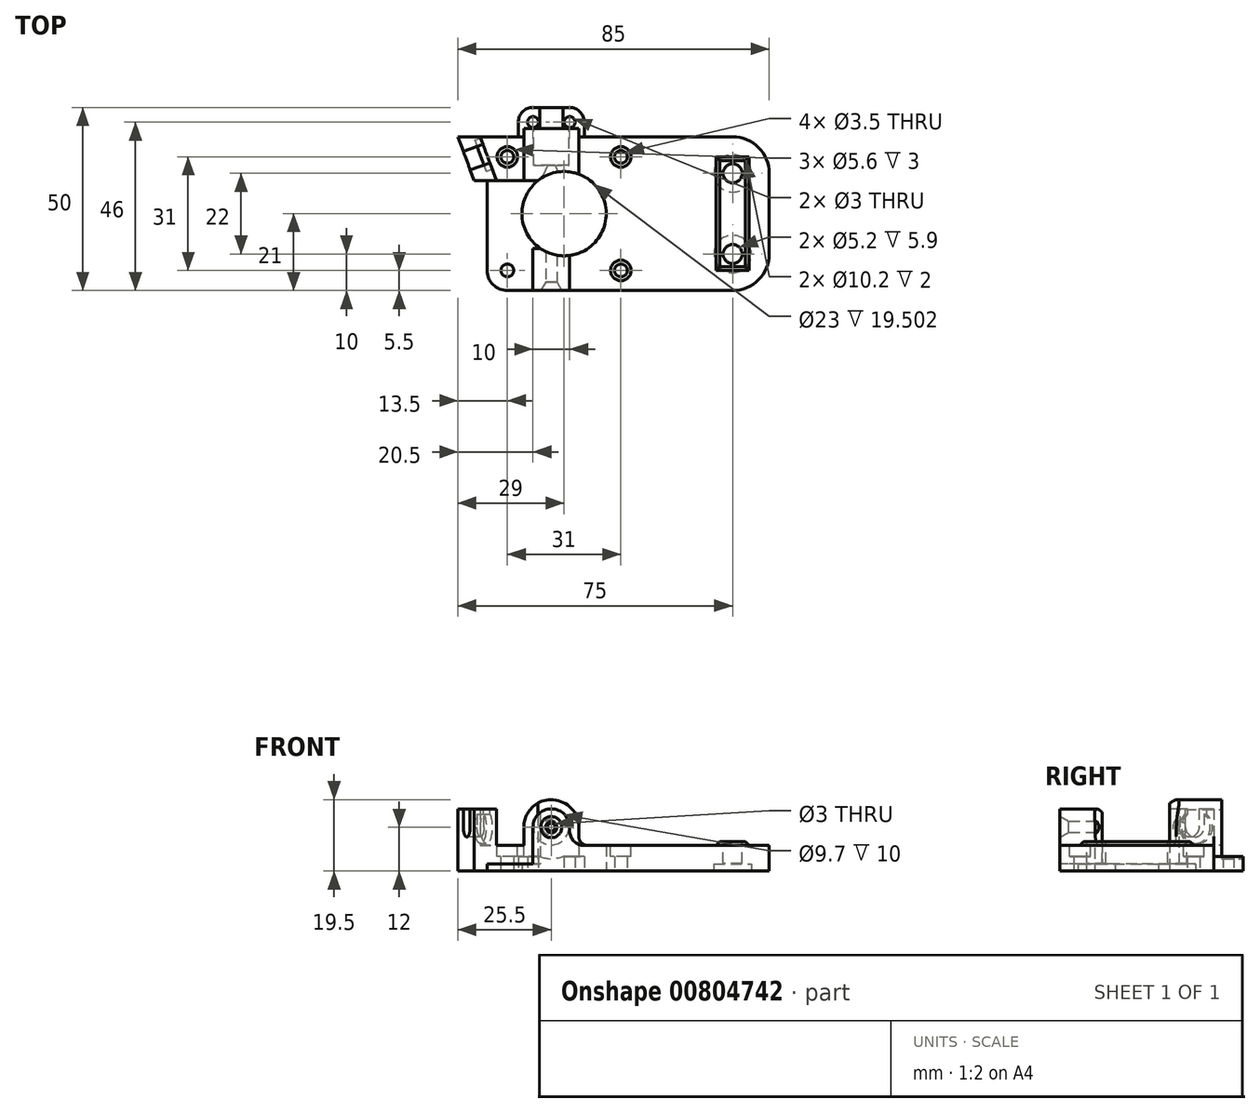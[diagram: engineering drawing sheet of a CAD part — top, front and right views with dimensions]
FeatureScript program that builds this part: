
annotation { "Feature Type Name" : "Feature", "Feature Type Description" : "" }
export const myFeature = defineFeature(function(context is Context, id is Id, definition is map)
    precondition{}
    {
        {
            var Q0;
            Q0=qCreatedBy(makeId("Top.planeOp"),FACE);
            var sketch = newSketch(context, id + "F0", { "sketchPlane" : qUnion([Q0])});
            skLineSegment(sketch, "E0.bottom", {"start": v(42.5, -21) * mm, "end": v(-34.5, -21) * mm});
            skLineSegment(sketch, "E0.top", {"start": v(42.5, 21) * mm, "end": v(-42.5, 21) * mm});
            skLineSegment(sketch, "E0.left", {"start": v(42.5, -21) * mm, "end": v(42.5, 21) * mm});
            skPoint(sketch, "E0.middle", {"position": v(0, 0) * mm});
            skLineSegment(sketch, "E1", {"start": v(-42.5, 21) * mm, "end": v(-38.06, 9) * mm});
            skLineSegment(sketch, "E2", {"start": v(-38.06, 9) * mm, "end": v(-34.5, 9) * mm});
            skLineSegment(sketch, "E3", {"start": v(-34.5, 9) * mm, "end": v(-34.5, -21) * mm});
            skPoint(sketch, "E4.orphan", {"position": v(-42.5, -21) * mm});
            skSolve(sketch);
        }
        {
            var Q0;
            Q0=makeQuery(id+"F0.imprint","IMPRINT",FACE,{"disambiguationData":[TD([[makeQuery(id+"F0.imprint","IMPRINT",EDGE,{"derivedFrom":sQuery(id+"F0.wireOp",EDGE,"E0.bottom")}),-1.0]])]});
            extrude(context, id + "F1", {"entities" : qUnion([Q0]), "depth" : 7 * mm, "offsetDistance" : 25 * mm});
        }
        {
            var Q0;
            Q0=makeQuery(id+"F1.opExtrude","SWEPT_FACE",FACE,{"disambiguationData":[OSD([sQuery(id+"F0.wireOp",EDGE,"E0.bottom")])]});
            var Q1;
            Q1=makeQuery(id+"F1.opExtrude","SWEPT_FACE",FACE,{"disambiguationData":[OSD([sQuery(id+"F0.wireOp",EDGE,"E0.top")])]});
            cPlane(context, id + "F2", {"entities" : qUnion([Q0, Q1]), "cplaneType" : CPlaneType.MID_PLANE, "offset" : 25 * mm, "width" : 150 * mm, "height" : 150 * mm});
        }
        {
            var Q0;
            Q0=makeQuery(id+"F1.opExtrude","SWEPT_FACE",FACE,{"disambiguationData":[OSD([sQuery(id+"F0.wireOp",EDGE,"E0.bottom")])]});
            var sketch = newSketch(context, id + "F3", { "sketchPlane" : qUnion([Q0])});
            skLineSegment(sketch, "E5", {"start": v(-22, 0) * mm, "end": v(-22, 12) * mm});
            skArc(sketch, "E6", {"start": v(-22, 12) * mm, "mid": v(-17, 17) * mm, "end": v(-12, 12) * mm});
            skLineSegment(sketch, "E7", {"start": v(-12, 12) * mm, "end": v(-12, 0) * mm});
            skLineSegment(sketch, "E8", {"start": v(-12, 0) * mm, "end": v(-22, 0) * mm});
            skSolve(sketch);
        }
        {
            var Q0;
            Q0=qSketchRegion(id+"F3",true);
            var Q1;
            Q1=qCreatedBy(id+"F2.planeOp",FACE);
            extrude(context, id + "F4", {"entities" : qUnion([Q0]), "operationType" : NewBodyOperationType.ADD, "endBound" : BoundingType.UP_TO_SURFACE, "oppositeDirection" : true, "depth" : 25 * mm, "endBoundEntityFace" : qUnion([Q1]), "offsetDistance" : 25 * mm});
        }
        {
            var Q0;
            Q0=makeQuery(id+"F4.boolean.opBoolean","MERGE",FACE,{"derivedFrom":[makeQuery(id+"F1.opExtrude","SWEPT_FACE",FACE,{"disambiguationData":[OSD([sQuery(id+"F0.wireOp",EDGE,"E0.bottom")])]}),makeQuery(id+"F4.opExtrude","CAP_FACE",FACE,{"disambiguationData":[OSD([sQuery(id+"F3.wireOp",EDGE,"E5"),sQuery(id+"F3.wireOp",EDGE,"E6"),sQuery(id+"F3.wireOp",EDGE,"E7"),sQuery(id+"F3.wireOp",EDGE,"E8")])],"isStart":true})]});
            var sketch = newSketch(context, id + "F5", { "sketchPlane" : qUnion([Q0])});
            skPoint(sketch, "E9", {"position": v(-17, 12) * mm});
            skSolve(sketch);
        }
        {
            var Q0;
            Q0=sQuery(id+"F5.wireOp",VERTEX,"E9");
            var Q1;
            Q1=makeQuery(id+"F1.opExtrude","SWEPT_BODY",BODY,{"disambiguationData":[OSD([sQuery(id+"F0.wireOp",EDGE,"E0.bottom"),sQuery(id+"F0.wireOp",EDGE,"E0.top"),sQuery(id+"F0.wireOp",EDGE,"E0.left"),sQuery(id+"F0.wireOp",EDGE,"E1"),sQuery(id+"F0.wireOp",EDGE,"E2"),sQuery(id+"F0.wireOp",EDGE,"E3")])]});
            hole(context, id + "F6", {"style" : HoleStyle.C_SINK, "endStyle" : HoleEndStyle.THROUGH, "standardTappedOrClearance" : lookupTablePath({ "standard" : "ISO", "size" : "3", "type" : "Drilled" }), "standardBlindInLast" : lookupTablePath({ "standard" : "ISO", "size" : "3", "type" : "Drilled" }), "holeDiameter" : 3 * mm, "cSinkDiameter" : 5.76 * mm, "cSinkAngle" : 60 * degree, "isTappedThrough" : true, "tappedDepth" : 12 * mm, "tapClearance" : 3, "locations" : qUnion([Q0]), "scope" : qUnion([Q1])});
        }
        {
            var Q0;
            Q0=qCreatedBy(id+"F2.planeOp",FACE);
            var sketch = newSketch(context, id + "F7", { "sketchPlane" : qUnion([Q0])});
            skLineSegment(sketch, "E10", {"start": v(-24.5, 0) * mm, "end": v(-24.5, 12) * mm});
            skArc(sketch, "E11", {"start": v(-24.5, 12) * mm, "mid": v(-17, 19.5) * mm, "end": v(-9.5, 12) * mm});
            skLineSegment(sketch, "E12", {"start": v(-9.5, 12) * mm, "end": v(-9.5, 0) * mm});
            skLineSegment(sketch, "E13", {"start": v(-9.5, 0) * mm, "end": v(-24.5, 0) * mm});
            skSolve(sketch);
        }
        {
            var Q0;
            Q0=makeQuery(id+"F7.imprint","IMPRINT",FACE,{"disambiguationData":[TD([[makeQuery(id+"F7.imprint","IMPRINT",EDGE,{"derivedFrom":sQuery(id+"F7.wireOp",EDGE,"E10")}),-1.0]])]});
            var Q1;
            Q1=sQuery(id+"F7.wireOp",EDGE,"E11");
            extrude(context, id + "F8", {"entities" : qUnion([Q0]), "operationType" : NewBodyOperationType.ADD, "surfaceEntities" : qUnion([Q1]), "oppositeDirection" : true, "depth" : 23.2 * mm, "offsetDistance" : 25 * mm});
        }
        {
            var Q0;
            Q0=makeQuery(id+"F8.boolean.opBoolean","MERGE",FACE,{"derivedFrom":[makeQuery(id+"F1.opExtrude","CAP_FACE",FACE,{"disambiguationData":[OSD([sQuery(id+"F0.wireOp",EDGE,"E0.bottom"),sQuery(id+"F0.wireOp",EDGE,"E0.top"),sQuery(id+"F0.wireOp",EDGE,"E0.left"),sQuery(id+"F0.wireOp",EDGE,"E1"),sQuery(id+"F0.wireOp",EDGE,"E2"),sQuery(id+"F0.wireOp",EDGE,"E3")])],"isStart":true}),makeQuery(id+"F8.opExtrude","SWEPT_FACE",FACE,{"disambiguationData":[OSD([sQuery(id+"F7.wireOp",EDGE,"E13")])]})]});
            var sketch = newSketch(context, id + "F9", { "sketchPlane" : qUnion([Q0])});
            skLineSegment(sketch, "E14", {"start": v(-8, -21) * mm, "end": v(-8, -29) * mm});
            skLineSegment(sketch, "E15", {"start": v(-8, -29) * mm, "end": v(-26, -29) * mm});
            skLineSegment(sketch, "E16", {"start": v(-26, -29) * mm, "end": v(-26, -21) * mm});
            skLineSegment(sketch, "E17", {"start": v(-8, -21) * mm, "end": v(-26, -21) * mm});
            skCircle(sketch, "E18", {"center": v(-12, -25) * mm, "radius": 1.5 * mm});
            skCircle(sketch, "E19", {"center": v(-22, -25) * mm, "radius": 1.5 * mm});
            skLineSegment(sketch, "E20", {"start": v(-12, -25) * mm, "end": v(-22, -25) * mm, "construction": true});
            skLineSegment(sketch, "E21", {"start": v(-17, -29) * mm, "end": v(-17, -25) * mm, "construction": true});
            skSolve(sketch);
        }
        {
            var Q0;
            {var subQ4=sQuery(id+"F9.wireOp",EDGE,"E14");Q0=makeQuery(id+"F9.imprint","IMPRINT",FACE,{"disambiguationData":[TD([[makeQuery(id+"F9.imprint","IMPRINT",EDGE,{"derivedFrom":subQ4}),-1.0]])]});}
            extrude(context, id + "F10", {"entities" : qUnion([Q0]), "operationType" : NewBodyOperationType.ADD, "oppositeDirection" : true, "depth" : 4 * mm, "offsetDistance" : 25 * mm});
        }
        {
            var Q0;
            Q0=makeQuery(id+"F10.opExtrude","SWEPT_FACE",FACE,{"disambiguationData":[OSD([sQuery(id+"F9.wireOp",EDGE,"E15")])]});
            var sketch = newSketch(context, id + "F11", { "sketchPlane" : qUnion([Q0])});
            skCircle(sketch, "E22", {"center": v(17, 12) * mm, "radius": 8.6 * mm});
            skSolve(sketch);
        }
        {
            var Q0;
            Q0=qSketchRegion(id+"F11",true);
            var Q1;
            Q1=makeQuery(id+"F8.opExtrude","CAP_FACE",FACE,{"disambiguationData":[OSD([sQuery(id+"F7.wireOp",EDGE,"E10"),sQuery(id+"F7.wireOp",EDGE,"E11"),sQuery(id+"F7.wireOp",EDGE,"E12"),sQuery(id+"F7.wireOp",EDGE,"E13")])],"isStart":false});
            extrude(context, id + "F12", {"entities" : qUnion([Q0]), "operationType" : NewBodyOperationType.REMOVE, "endBound" : BoundingType.UP_TO_SURFACE, "oppositeDirection" : true, "depth" : 25 * mm, "endBoundEntityFace" : qUnion([Q1]), "offsetDistance" : 25 * mm});
        }
        {
            var Q0;
            {var subQ0=sQuery(id+"F7.wireOp",EDGE,"E13");var subQ1=sQuery(id+"F7.wireOp",EDGE,"E12");var subQ2=sQuery(id+"F7.wireOp",EDGE,"E11");var subQ3=sQuery(id+"F7.wireOp",EDGE,"E10");Q0=makeQuery(id+"F12.boolean.opBoolean","MERGE",FACE,{"derivedFrom":[makeQuery(id+"F8.opExtrude","CAP_FACE",FACE,{"disambiguationData":[OSD([subQ3,subQ2,subQ1,subQ0])],"isStart":false}),makeQuery(id+"F12.opExtrude","CAP_FACE",FACE,{"disambiguationData":[OSD([subQ3,subQ2,subQ1,subQ0])],"isStart":false})]});}
            var sketch = newSketch(context, id + "F13", { "sketchPlane" : qUnion([Q0])});
            skCircle(sketch, "E23", {"center": v(17, 12) * mm, "radius": 4.85 * mm});
            skSolve(sketch);
        }
        {
            var Q0;
            Q0=qSketchRegion(id+"F13",true);
            extrude(context, id + "F14", {"entities" : qUnion([Q0]), "operationType" : NewBodyOperationType.REMOVE, "oppositeDirection" : true, "depth" : 10 * mm, "offsetDistance" : 25 * mm});
        }
        {
            var Q0;
            {var subQ0=sQuery(id+"F0.wireOp",EDGE,"E2");var subQ2=sQuery(id+"F0.wireOp",EDGE,"E0.top");var subQ4=sQuery(id+"F0.wireOp",EDGE,"E1");var subQ5=sQuery(id+"F0.wireOp",EDGE,"E0.bottom");var subQ6=sQuery(id+"F0.wireOp",EDGE,"E3");Q0=makeQuery(id+"F8.boolean.opBoolean","SPLIT",FACE,{"disambiguationData":[TD([makeQuery(id+"F1.opExtrude","SWEPT_FACE",FACE,{"disambiguationData":[OSD([subQ4])]})])],"derivedFrom":makeQuery(id+"F1.opExtrude","CAP_FACE",FACE,{"disambiguationData":[OSD([subQ5,subQ2,sQuery(id+"F0.wireOp",EDGE,"E0.left"),subQ4,subQ0,subQ6])],"isStart":false})});}
            var sketch = newSketch(context, id + "F15", { "sketchPlane" : qUnion([Q0])});
            skLineSegment(sketch, "E24", {"start": v(-42.5, 21) * mm, "end": v(-36.42, 21) * mm});
            skLineSegment(sketch, "E25", {"start": v(-36.42, 21) * mm, "end": v(-31.98, 9) * mm});
            skLineSegment(sketch, "E26", {"start": v(-31.98, 9) * mm, "end": v(-38.06, 9) * mm});
            skLineSegment(sketch, "E27", {"start": v(-38.06, 9) * mm, "end": v(-42.5, 21) * mm});
            skSolve(sketch);
        }
        {
            var Q0;
            Q0=qSketchRegion(id+"F15",true);
            extrude(context, id + "F16", {"entities" : qUnion([Q0]), "operationType" : NewBodyOperationType.ADD, "depth" : 10 * mm, "offsetDistance" : 25 * mm});
        }
        {
            var Q0;
            Q0=makeQuery(id+"F16.boolean.opBoolean","MERGE",FACE,{"derivedFrom":[makeQuery(id+"F1.opExtrude","SWEPT_FACE",FACE,{"disambiguationData":[OSD([sQuery(id+"F0.wireOp",EDGE,"E1")])]}),makeQuery(id+"F16.opExtrude","SWEPT_FACE",FACE,{"disambiguationData":[OSD([sQuery(id+"F15.wireOp",EDGE,"E27")])]})]});
            var sketch = newSketch(context, id + "F17", { "sketchPlane" : qUnion([Q0])});
            skLineSegment(sketch, "E28", {"start": v(-30.14, 17) * mm, "end": v(-30.14, 12) * mm});
            skArc(sketch, "E29", {"start": v(-30.14, 12) * mm, "mid": v(-27.44, 9.3) * mm, "end": v(-24.74, 12) * mm});
            skLineSegment(sketch, "E30", {"start": v(-24.74, 12) * mm, "end": v(-24.74, 17) * mm});
            skLineSegment(sketch, "E31", {"start": v(-30.14, 17) * mm, "end": v(-24.74, 17) * mm});
            skSolve(sketch);
        }
        {
            var Q0;
            Q0=qSketchRegion(id+"F17",true);
            extrude(context, id + "F18", {"entities" : qUnion([Q0]), "operationType" : NewBodyOperationType.REMOVE, "endBound" : BoundingType.UP_TO_NEXT, "oppositeDirection" : true, "depth" : 25 * mm, "offsetDistance" : 25 * mm});
        }
        {
            var Q0;
            Q0=makeQuery(id+"F16.opExtrude","SWEPT_FACE",FACE,{"disambiguationData":[OSD([sQuery(id+"F15.wireOp",EDGE,"E25")])]});
            var sketch = newSketch(context, id + "F19", { "sketchPlane" : qUnion([Q0])});
            skCircle(sketch, "E32", {"center": v(27.44, 12) * mm, "radius": 4.5 * mm});
            skSolve(sketch);
        }
        {
            var Q0;
            Q0=qSketchRegion(id+"F19",true);
            var Q1;
            Q1=makeQuery(id+"F16.boolean.opBoolean","MERGE",FACE,{"derivedFrom":[makeQuery(id+"F1.opExtrude","SWEPT_FACE",FACE,{"disambiguationData":[OSD([sQuery(id+"F0.wireOp",EDGE,"E1")])]}),makeQuery(id+"F16.opExtrude","SWEPT_FACE",FACE,{"disambiguationData":[OSD([sQuery(id+"F15.wireOp",EDGE,"E27")])]})]});
            extrude(context, id + "F20", {"entities" : qUnion([Q0]), "operationType" : NewBodyOperationType.REMOVE, "endBound" : BoundingType.UP_TO_SURFACE, "oppositeDirection" : true, "depth" : .5 * mm, "endBoundEntityFace" : qUnion([Q1]), "hasOffset" : true, "offsetDistance" : 4 * mm});
        }
        {
            var Q0;
            {var subQ1=sQuery(id+"F0.wireOp",EDGE,"E0.left");var subQ2=sQuery(id+"F0.wireOp",EDGE,"E0.top");var subQ4=sQuery(id+"F0.wireOp",EDGE,"E0.bottom");Q0=makeQuery(id+"F8.boolean.opBoolean","SPLIT",FACE,{"disambiguationData":[TD([makeQuery(id+"F1.opExtrude","SWEPT_FACE",FACE,{"disambiguationData":[OSD([subQ1])]})])],"derivedFrom":makeQuery(id+"F1.opExtrude","CAP_FACE",FACE,{"disambiguationData":[OSD([subQ4,subQ2,subQ1,sQuery(id+"F0.wireOp",EDGE,"E1"),sQuery(id+"F0.wireOp",EDGE,"E2"),sQuery(id+"F0.wireOp",EDGE,"E3")])],"isStart":false})});}
            var sketch = newSketch(context, id + "F21", { "sketchPlane" : qUnion([Q0])});
            skLineSegment(sketch, "E33.bottom", {"start": v(37, -15.5) * mm, "end": v(28, -15.5) * mm});
            skLineSegment(sketch, "E33.top", {"start": v(37, 15.5) * mm, "end": v(28, 15.5) * mm});
            skLineSegment(sketch, "E33.left", {"start": v(37, -15.5) * mm, "end": v(37, 15.5) * mm});
            skLineSegment(sketch, "E33.right", {"start": v(28, -15.5) * mm, "end": v(28, 15.5) * mm});
            skPoint(sketch, "E33.middle", {"position": v(32.5, 0) * mm});
            skSolve(sketch);
        }
        {
            var Q0;
            Q0=qSketchRegion(id+"F21",true);
            extrude(context, id + "F22", {"entities" : qUnion([Q0]), "operationType" : NewBodyOperationType.ADD, "depth" : 1 * mm, "offsetDistance" : 25 * mm});
        }
        {
            var Q0;
            Q0=makeQuery(id+"F22.opExtrude","CAP_EDGE",EDGE,{"disambiguationData":[OSD([sQuery(id+"F21.wireOp",EDGE,"E33.left")])],"isStart":false});
            var Q1;
            Q1=makeQuery(id+"F22.opExtrude","CAP_EDGE",EDGE,{"disambiguationData":[OSD([sQuery(id+"F21.wireOp",EDGE,"E33.top")])],"isStart":false});
            var Q2;
            Q2=makeQuery(id+"F22.opExtrude","CAP_EDGE",EDGE,{"disambiguationData":[OSD([sQuery(id+"F21.wireOp",EDGE,"E33.right")])],"isStart":false});
            var Q3;
            Q3=makeQuery(id+"F22.opExtrude","CAP_EDGE",EDGE,{"disambiguationData":[OSD([sQuery(id+"F21.wireOp",EDGE,"E33.bottom")])],"isStart":false});
            chamfer(context, id + "F23", {"entities" : qUnion([Q0, Q1, Q2, Q3]), "width" : 1 * mm, "tangentPropagation" : true});
        }
        {
            var Q0;
            Q0=makeQuery(id+"F22.opExtrude","CAP_FACE",FACE,{"disambiguationData":[OSD([sQuery(id+"F21.wireOp",EDGE,"E33.bottom"),sQuery(id+"F21.wireOp",EDGE,"E33.top"),sQuery(id+"F21.wireOp",EDGE,"E33.left"),sQuery(id+"F21.wireOp",EDGE,"E33.right")])],"isStart":false});
            var sketch = newSketch(context, id + "F24", { "sketchPlane" : qUnion([Q0])});
            skCircle(sketch, "E34", {"center": v(32.5, -11) * mm, "radius": 2.6 * mm});
            skPoint(sketch, "E34.centerSnap0", {"position": v(32.5, -14.5) * mm});
            skCircle(sketch, "E35", {"center": v(32.5, 11) * mm, "radius": 2.6 * mm});
            skLineSegment(sketch, "E36", {"start": v(32.5, -11) * mm, "end": v(32.5, 11) * mm, "construction": true});
            skLineSegment(sketch, "E37", {"start": v(36, 0) * mm, "end": v(32.5, 0) * mm, "construction": true});
            skSolve(sketch);
        }
        {
            var Q0;
            Q0=qSketchRegion(id+"F24",true);
            extrude(context, id + "F25", {"entities" : qUnion([Q0]), "operationType" : NewBodyOperationType.REMOVE, "oppositeDirection" : true, "depth" : 5.9 * mm, "offsetDistance" : 25 * mm});
        }
        {
            var Q0;
            {var subQ0=sQuery(id+"F7.wireOp",EDGE,"E13");Q0=makeQuery(id+"F10.boolean.opBoolean","MERGE",FACE,{"derivedFrom":[makeQuery(id+"F8.boolean.opBoolean","MERGE",FACE,{"derivedFrom":[makeQuery(id+"F1.opExtrude","CAP_FACE",FACE,{"disambiguationData":[OSD([sQuery(id+"F0.wireOp",EDGE,"E0.bottom"),sQuery(id+"F0.wireOp",EDGE,"E0.top"),sQuery(id+"F0.wireOp",EDGE,"E0.left"),sQuery(id+"F0.wireOp",EDGE,"E1"),sQuery(id+"F0.wireOp",EDGE,"E2"),sQuery(id+"F0.wireOp",EDGE,"E3")])],"isStart":true}),makeQuery(id+"F8.opExtrude","SWEPT_FACE",FACE,{"disambiguationData":[OSD([subQ0])]})]}),makeQuery(id+"F10.opExtrude","CAP_FACE",FACE,{"disambiguationData":[OSD([sQuery(id+"F7.wireOp",EDGE,"E10"),sQuery(id+"F7.wireOp",EDGE,"E12"),subQ0,sQuery(id+"F9.wireOp",EDGE,"E14"),sQuery(id+"F9.wireOp",EDGE,"E15"),sQuery(id+"F9.wireOp",EDGE,"E16"),sQuery(id+"F9.wireOp",EDGE,"E17"),sQuery(id+"F9.wireOp",EDGE,"E18"),sQuery(id+"F9.wireOp",EDGE,"E19")])],"isStart":true})]});}
            var sketch = newSketch(context, id + "F26", { "sketchPlane" : qUnion([Q0])});
            skCircle(sketch, "E38", {"center": v(32.5, -11) * mm, "radius": 5.1 * mm});
            skCircle(sketch, "E39", {"center": v(32.5, 11) * mm, "radius": 5.1 * mm});
            skSolve(sketch);
        }
        {
            var Q0;
            Q0=qSketchRegion(id+"F26",true);
            extrude(context, id + "F27", {"entities" : qUnion([Q0]), "operationType" : NewBodyOperationType.REMOVE, "oppositeDirection" : true, "depth" : 2 * mm, "offsetDistance" : 25 * mm});
        }
        {
            var Q0;
            {var subQ0=sQuery(id+"F7.wireOp",EDGE,"E13");Q0=makeQuery(id+"F10.boolean.opBoolean","MERGE",FACE,{"derivedFrom":[makeQuery(id+"F8.boolean.opBoolean","MERGE",FACE,{"derivedFrom":[makeQuery(id+"F1.opExtrude","CAP_FACE",FACE,{"disambiguationData":[OSD([sQuery(id+"F0.wireOp",EDGE,"E0.bottom"),sQuery(id+"F0.wireOp",EDGE,"E0.top"),sQuery(id+"F0.wireOp",EDGE,"E0.left"),sQuery(id+"F0.wireOp",EDGE,"E1"),sQuery(id+"F0.wireOp",EDGE,"E2"),sQuery(id+"F0.wireOp",EDGE,"E3")])],"isStart":true}),makeQuery(id+"F8.opExtrude","SWEPT_FACE",FACE,{"disambiguationData":[OSD([subQ0])]})]}),makeQuery(id+"F10.opExtrude","CAP_FACE",FACE,{"disambiguationData":[OSD([sQuery(id+"F7.wireOp",EDGE,"E10"),sQuery(id+"F7.wireOp",EDGE,"E12"),subQ0,sQuery(id+"F9.wireOp",EDGE,"E14"),sQuery(id+"F9.wireOp",EDGE,"E15"),sQuery(id+"F9.wireOp",EDGE,"E16"),sQuery(id+"F9.wireOp",EDGE,"E17"),sQuery(id+"F9.wireOp",EDGE,"E18"),sQuery(id+"F9.wireOp",EDGE,"E19")])],"isStart":true})]});}
            var sketch = newSketch(context, id + "F28", { "sketchPlane" : qUnion([Q0])});
            skLineSegment(sketch, "E40.bottom", {"start": v(2, -15.5) * mm, "end": v(-29, -15.5) * mm, "construction": true});
            skLineSegment(sketch, "E40.top", {"start": v(2, 15.5) * mm, "end": v(-29, 15.5) * mm, "construction": true});
            skLineSegment(sketch, "E40.left", {"start": v(2, -15.5) * mm, "end": v(2, 15.5) * mm, "construction": true});
            skLineSegment(sketch, "E40.right", {"start": v(-29, -15.5) * mm, "end": v(-29, 15.5) * mm, "construction": true});
            skPoint(sketch, "E40.middle", {"position": v(-13.5, 0) * mm});
            skPoint(sketch, "E41", {"position": v(2, -15.5) * mm});
            skPoint(sketch, "E42", {"position": v(-29, -15.5) * mm});
            skPoint(sketch, "E43", {"position": v(-29, 15.5) * mm});
            skPoint(sketch, "E44", {"position": v(2, 15.5) * mm});
            skSolve(sketch);
        }
        {
            var Q0;
            Q0=sQuery(id+"F28.wireOp",VERTEX,"E41");
            var Q1;
            Q1=sQuery(id+"F28.wireOp",VERTEX,"E42");
            var Q2;
            Q2=sQuery(id+"F28.wireOp",VERTEX,"E43");
            var Q3;
            Q3=sQuery(id+"F28.wireOp",VERTEX,"E44");
            var Q4;
            Q4=makeQuery(id+"F1.opExtrude","SWEPT_BODY",BODY,{"disambiguationData":[OSD([sQuery(id+"F0.wireOp",EDGE,"E0.bottom"),sQuery(id+"F0.wireOp",EDGE,"E0.top"),sQuery(id+"F0.wireOp",EDGE,"E0.left"),sQuery(id+"F0.wireOp",EDGE,"E1"),sQuery(id+"F0.wireOp",EDGE,"E2"),sQuery(id+"F0.wireOp",EDGE,"E3")])]});
            hole(context, id + "F29", {"style" : HoleStyle.SIMPLE, "endStyle" : HoleEndStyle.THROUGH, "standardTappedOrClearance" : lookupTablePath({ "standard" : "ISO", "size" : "3.5", "type" : "Drilled" }), "standardBlindInLast" : lookupTablePath({ "standard" : "ISO", "size" : "3.5", "type" : "Drilled" }), "holeDiameter" : 3.5 * mm, "isTappedThrough" : true, "tappedDepth" : 12 * mm, "tapClearance" : 3, "locations" : qUnion([Q0, Q1, Q2, Q3]), "scope" : qUnion([Q4])});
        }
        {
            var Q0;
            {var subQ1=sQuery(id+"F0.wireOp",EDGE,"E0.left");Q0=makeQuery(id+"F28.imprint","IMPRINT",FACE,{"disambiguationData":[TD([[makeQuery(id+"F28.imprint","IMPRINT",EDGE,{"derivedFrom":makeQuery(id+"F1.opExtrude","CAP_EDGE",EDGE,{"disambiguationData":[OSD([subQ1])],"isStart":true})}),-1.0]])]});}
            var sketch = newSketch(context, id + "F30", { "sketchPlane" : qUnion([Q0])});
            skCircle(sketch, "E45", {"center": v(-13.5, 0) * mm, "radius": 11.5 * mm});
            skSolve(sketch);
        }
        {
            var Q0;
            Q0=qSketchRegion(id+"F30",true);
            extrude(context, id + "F31", {"entities" : qUnion([Q0]), "operationType" : NewBodyOperationType.REMOVE, "endBound" : BoundingType.UP_TO_NEXT, "oppositeDirection" : true, "depth" : 25 * mm, "offsetDistance" : 25 * mm});
        }
        {
            var Q0;
            {var subQ0=sQuery(id+"F0.wireOp",EDGE,"E2");var subQ2=sQuery(id+"F0.wireOp",EDGE,"E0.top");var subQ4=sQuery(id+"F0.wireOp",EDGE,"E1");var subQ5=sQuery(id+"F0.wireOp",EDGE,"E0.bottom");var subQ6=sQuery(id+"F0.wireOp",EDGE,"E3");Q0=makeQuery(id+"F8.boolean.opBoolean","SPLIT",FACE,{"disambiguationData":[TD([makeQuery(id+"F1.opExtrude","SWEPT_FACE",FACE,{"disambiguationData":[OSD([subQ4])]})])],"derivedFrom":makeQuery(id+"F1.opExtrude","CAP_FACE",FACE,{"disambiguationData":[OSD([subQ5,subQ2,sQuery(id+"F0.wireOp",EDGE,"E0.left"),subQ4,subQ0,subQ6])],"isStart":false})});}
            var sketch = newSketch(context, id + "F32", { "sketchPlane" : qUnion([Q0])});
            skLineSegment(sketch, "E46", {"start": v(-34.5, -21) * mm, "end": v(-22, -21) * mm});
            skLineSegment(sketch, "E47", {"start": v(-22, -21) * mm, "end": v(-22, -9.5) * mm});
            skLineSegment(sketch, "E48", {"start": v(-22, -9.5) * mm, "end": v(-13.5, -9.5) * mm});
            skLineSegment(sketch, "E49", {"start": v(-13.5, -9.5) * mm, "end": v(-13.5, 9) * mm});
            skLineSegment(sketch, "E50", {"start": v(-13.5, 9) * mm, "end": v(-34.5, 9) * mm});
            skLineSegment(sketch, "E51", {"start": v(-34.5, 9) * mm, "end": v(-34.5, -21) * mm});
            skSolve(sketch);
        }
        {
            var Q0;
            Q0=qSketchRegion(id+"F32",true);
            var Q1;
            {var subQ0=sQuery(id+"F7.wireOp",EDGE,"E13");Q1=makeQuery(id+"F10.boolean.opBoolean","MERGE",FACE,{"derivedFrom":[makeQuery(id+"F8.boolean.opBoolean","MERGE",FACE,{"derivedFrom":[makeQuery(id+"F1.opExtrude","CAP_FACE",FACE,{"disambiguationData":[OSD([sQuery(id+"F0.wireOp",EDGE,"E0.bottom"),sQuery(id+"F0.wireOp",EDGE,"E0.top"),sQuery(id+"F0.wireOp",EDGE,"E0.left"),sQuery(id+"F0.wireOp",EDGE,"E1"),sQuery(id+"F0.wireOp",EDGE,"E2"),sQuery(id+"F0.wireOp",EDGE,"E3")])],"isStart":true}),makeQuery(id+"F8.opExtrude","SWEPT_FACE",FACE,{"disambiguationData":[OSD([subQ0])]})]}),makeQuery(id+"F10.opExtrude","CAP_FACE",FACE,{"disambiguationData":[OSD([sQuery(id+"F7.wireOp",EDGE,"E10"),sQuery(id+"F7.wireOp",EDGE,"E12"),subQ0,sQuery(id+"F9.wireOp",EDGE,"E14"),sQuery(id+"F9.wireOp",EDGE,"E15"),sQuery(id+"F9.wireOp",EDGE,"E16"),sQuery(id+"F9.wireOp",EDGE,"E17"),sQuery(id+"F9.wireOp",EDGE,"E18"),sQuery(id+"F9.wireOp",EDGE,"E19")])],"isStart":true})]});}
            extrude(context, id + "F33", {"entities" : qUnion([Q0]), "operationType" : NewBodyOperationType.REMOVE, "endBound" : BoundingType.UP_TO_SURFACE, "oppositeDirection" : true, "depth" : 25 * mm, "endBoundEntityFace" : qUnion([Q1]), "hasOffset" : true, "offsetDistance" : 2 * mm, "hasSecondDirection" : true, "secondDirectionBound" : SecondDirectionBoundingType.THROUGH_ALL, "secondDirectionOppositeDirection" : false, "secondDirectionDepth" : 25 * mm});
        }
        {
            var Q0;
            Q0=makeQuery(id+"F14.boolean.opBoolean","COPY",FACE,{"derivedFrom":makeQuery(id+"F14.opExtrude","CAP_FACE",FACE,{"disambiguationData":[OSD([sQuery(id+"F13.wireOp",EDGE,"E23")])],"isStart":false})});
            var sketch = newSketch(context, id + "F34", { "sketchPlane" : qUnion([Q0])});
            skCircle(sketch, "E52", {"center": v(17, 12) * mm, "radius": 1.05 * mm});
            skSolve(sketch);
        }
        {
            var Q0;
            Q0=makeQuery(id+"F34.imprint","IMPRINT",FACE,{"disambiguationData":[TD([[makeQuery(id+"F34.imprint","IMPRINT",EDGE,{"derivedFrom":sQuery(id+"F34.wireOp",EDGE,"E52")}),1.0]])]});
            extrude(context, id + "F35", {"entities" : qUnion([Q0]), "operationType" : NewBodyOperationType.REMOVE, "endBound" : BoundingType.UP_TO_NEXT, "oppositeDirection" : true, "depth" : 25 * mm, "offsetDistance" : 25 * mm, "hasDraft" : true, "draftAngle" : 22.6 * degree});
        }
        {
            var Q0;
            {var subQ1=sQuery(id+"F0.wireOp",EDGE,"E0.left");var subQ2=sQuery(id+"F0.wireOp",EDGE,"E0.top");var subQ4=sQuery(id+"F0.wireOp",EDGE,"E0.bottom");Q0=makeQuery(id+"F8.boolean.opBoolean","SPLIT",FACE,{"disambiguationData":[TD([makeQuery(id+"F1.opExtrude","SWEPT_FACE",FACE,{"disambiguationData":[OSD([subQ1])]})])],"derivedFrom":makeQuery(id+"F1.opExtrude","CAP_FACE",FACE,{"disambiguationData":[OSD([subQ4,subQ2,subQ1,sQuery(id+"F0.wireOp",EDGE,"E1"),sQuery(id+"F0.wireOp",EDGE,"E2"),sQuery(id+"F0.wireOp",EDGE,"E3")])],"isStart":false})});}
            var sketch = newSketch(context, id + "F36", { "sketchPlane" : qUnion([Q0])});
            skCircle(sketch, "E53", {"center": v(2, -15.5) * mm, "radius": 2.8 * mm});
            skCircle(sketch, "E54", {"center": v(2, 15.5) * mm, "radius": 2.8 * mm});
            skCircle(sketch, "E55", {"center": v(-29, 15.5) * mm, "radius": 2.8 * mm});
            skSolve(sketch);
        }
        {
            var Q0;
            Q0=qSketchRegion(id+"F36",true);
            extrude(context, id + "F37", {"entities" : qUnion([Q0]), "operationType" : NewBodyOperationType.REMOVE, "oppositeDirection" : true, "depth" : 3 * mm, "offsetDistance" : 25 * mm});
        }
        {
            var Q0;
            Q0=makeQuery(id+"F4.boolean.opBoolean","INTERSECT",EDGE,{"derivedFrom":[makeQuery(id+"F1.opExtrude","CAP_FACE",FACE,{"disambiguationData":[OSD([sQuery(id+"F0.wireOp",EDGE,"E0.bottom"),sQuery(id+"F0.wireOp",EDGE,"E0.top"),sQuery(id+"F0.wireOp",EDGE,"E0.left"),sQuery(id+"F0.wireOp",EDGE,"E1"),sQuery(id+"F0.wireOp",EDGE,"E2"),sQuery(id+"F0.wireOp",EDGE,"E3")])],"isStart":false}),makeQuery(id+"F4.opExtrude","SWEPT_FACE",FACE,{"disambiguationData":[OSD([sQuery(id+"F3.wireOp",EDGE,"E7")])]})]});
            var Q1;
            Q1=makeQuery(id+"F10.opExtrude","SWEPT_EDGE",EDGE,{"disambiguationData":[OSD([sQuery(id+"F9.wireOp",EDGE,"E14"),sQuery(id+"F9.wireOp",EDGE,"E15")])]});
            var Q2;
            Q2=makeQuery(id+"F10.opExtrude","SWEPT_EDGE",EDGE,{"disambiguationData":[OSD([sQuery(id+"F9.wireOp",EDGE,"E15"),sQuery(id+"F9.wireOp",EDGE,"E16")])]});
            fillet(context, id + "F38", {"entities" : qUnion([Q0, Q1, Q2]), "radius" : 4 * mm, "tangentPropagation" : true, "allowEdgeOverflow" : false});
        }
        {
            var Q0;
            Q0=makeQuery(id+"F1.opExtrude","SWEPT_EDGE",EDGE,{"disambiguationData":[OSD([sQuery(id+"F0.wireOp",EDGE,"E0.bottom"),sQuery(id+"F0.wireOp",EDGE,"E3")])]});
            fillet(context, id + "F39", {"entities" : qUnion([Q0]), "radius" : 5.5 * mm, "tangentPropagation" : true, "allowEdgeOverflow" : false});
        }
        {
            var Q0;
            Q0=makeQuery(id+"F8.boolean.opBoolean","INTERSECT",EDGE,{"derivedFrom":[makeQuery(id+"F1.opExtrude","CAP_FACE",FACE,{"disambiguationData":[OSD([sQuery(id+"F0.wireOp",EDGE,"E0.bottom"),sQuery(id+"F0.wireOp",EDGE,"E0.top"),sQuery(id+"F0.wireOp",EDGE,"E0.left"),sQuery(id+"F0.wireOp",EDGE,"E1"),sQuery(id+"F0.wireOp",EDGE,"E2"),sQuery(id+"F0.wireOp",EDGE,"E3")])],"isStart":false}),makeQuery(id+"F8.opExtrude","SWEPT_FACE",FACE,{"disambiguationData":[OSD([sQuery(id+"F7.wireOp",EDGE,"E12")])]})]});
            fillet(context, id + "F40", {"entities" : qUnion([Q0]), "radius" : 2.5 * mm, "tangentPropagation" : true, "allowEdgeOverflow" : false});
        }
        {
            var Q0;
            Q0=makeQuery(id+"F1.opExtrude","SWEPT_EDGE",EDGE,{"disambiguationData":[OSD([sQuery(id+"F0.wireOp",EDGE,"E0.top"),sQuery(id+"F0.wireOp",EDGE,"E0.left")])]});
            var Q1;
            Q1=makeQuery(id+"F1.opExtrude","SWEPT_EDGE",EDGE,{"disambiguationData":[OSD([sQuery(id+"F0.wireOp",EDGE,"E0.bottom"),sQuery(id+"F0.wireOp",EDGE,"E0.left")])]});
            fillet(context, id + "F41", {"entities" : qUnion([Q0, Q1]), "radius" : 10 * mm, "tangentPropagation" : true, "allowEdgeOverflow" : false});
        }
    });
